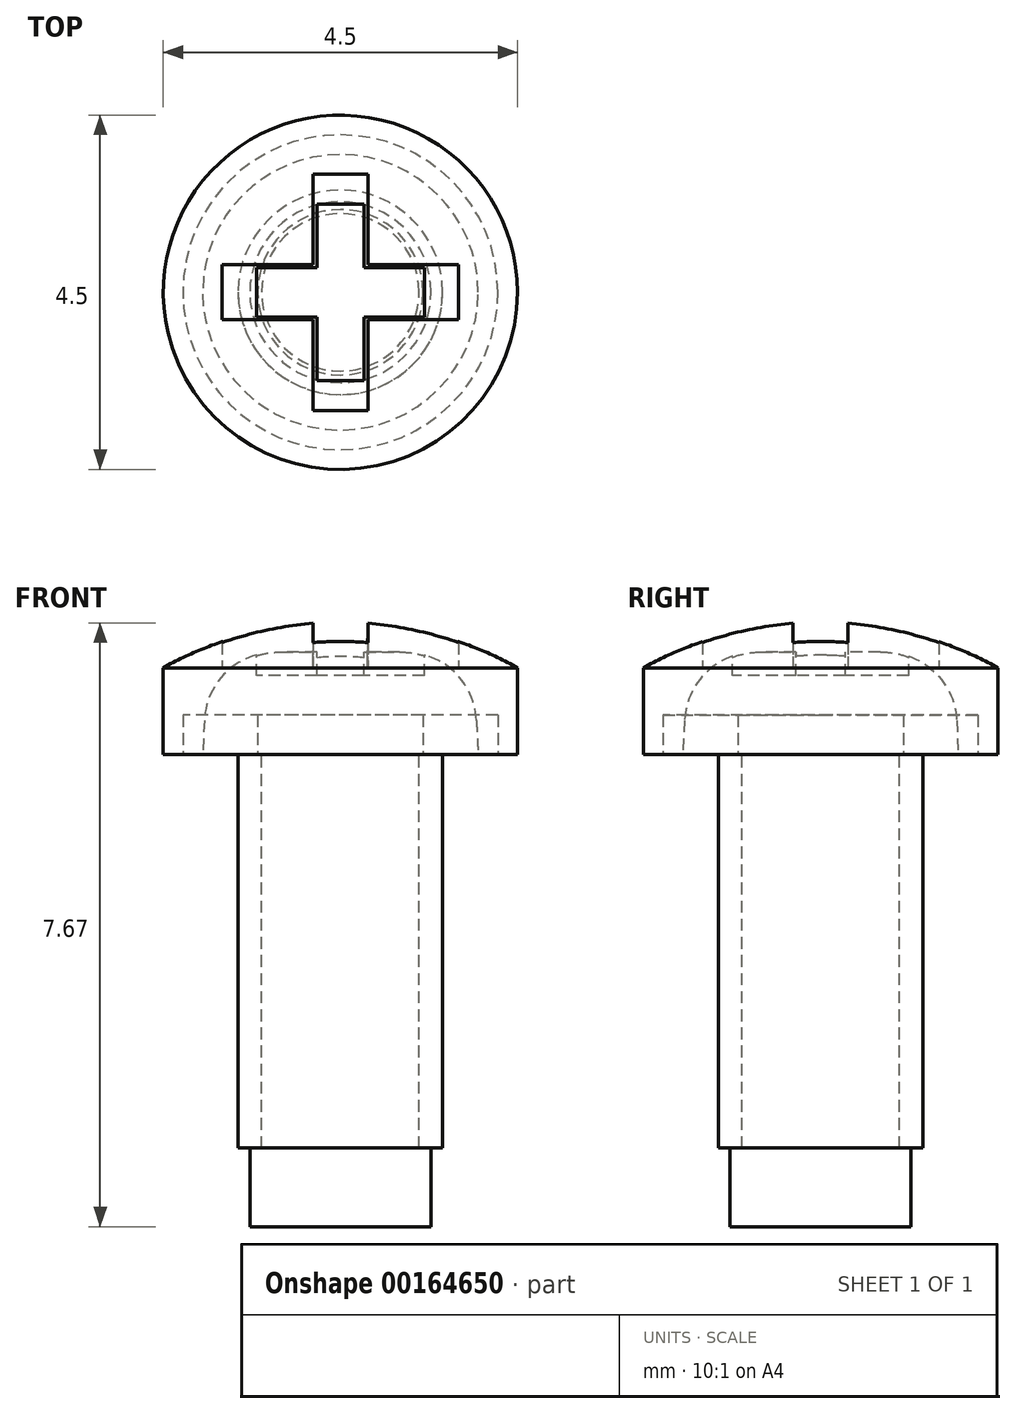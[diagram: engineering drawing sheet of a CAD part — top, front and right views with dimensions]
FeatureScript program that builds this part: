
annotation { "Feature Type Name" : "Feature", "Feature Type Description" : "" }
export const myFeature = defineFeature(function(context is Context, id is Id, definition is map)
    precondition{}
    {
        {
            var Q0;
            Q0=qCreatedBy(makeId("Front.planeOp"),FACE);
            var sketch = newSketch(context, id + "F0", { "sketchPlane" : qUnion([Q0])});
            skLineSegment(sketch, "E0", {"start": v(0, 1.5) * mm, "end": v(0, 0) * mm});
            skLineSegment(sketch, "E1", {"start": v(0, 0) * mm, "end": v(2, 0) * mm});
            skLineSegment(sketch, "E2", {"start": v(2, 0) * mm, "end": v(2, 0.7) * mm});
            skArc(sketch, "E3", {"start": v(2, 0.7) * mm, "mid": v(1.09, 1.31) * mm, "end": v(0, 1.5) * mm});
            skSolve(sketch);
        }
        {
            var Q0;
            Q0=qSketchRegion(id+"F0",true);
            var Q1;
            Q1=sQuery(id+"F0.wireOp",EDGE,"E0");
            revolve(context, id + "F1", {"entities" : qUnion([Q0]), "axis" : qUnion([Q1]), "revolveType" : RevolveType.FULL});
        }
        {
            var Q0;
            Q0=qCreatedBy(makeId("Top.planeOp"),FACE);
            cPlane(context, id + "F2", {"entities" : qUnion([Q0]), "cplaneType" : CPlaneType.OFFSET, "offset" : 1 * mm, "width" : 150 * mm, "height" : 150 * mm});
        }
        {
            var Q0;
            Q0=qCreatedBy(id+"F2.planeOp",FACE);
            var sketch = newSketch(context, id + "F3", { "sketchPlane" : qUnion([Q0])});
            skLineSegment(sketch, "E4.rect.bottom", {"start": v(0.34, 1.34) * mm, "end": v(-0.34, 1.34) * mm});
            skLineSegment(sketch, "E4.rect.top", {"start": v(0.34, -1.34) * mm, "end": v(-0.34, -1.34) * mm});
            skLineSegment(sketch, "E4.rect.left", {"start": v(0.34, 1.34) * mm, "end": v(0.34, -1.34) * mm});
            skLineSegment(sketch, "E4.rect.right", {"start": v(-0.34, 1.34) * mm, "end": v(-0.34, -1.34) * mm});
            skPoint(sketch, "E4.rect.middle", {"position": v(0, 0) * mm});
            skLineSegment(sketch, "E5.rect.bottom", {"start": v(1.32, 0.3) * mm, "end": v(-1.32, 0.3) * mm});
            skLineSegment(sketch, "E5.rect.top", {"start": v(1.32, -0.3) * mm, "end": v(-1.32, -0.3) * mm});
            skLineSegment(sketch, "E5.rect.left", {"start": v(1.32, 0.3) * mm, "end": v(1.32, -0.3) * mm});
            skLineSegment(sketch, "E5.rect.right", {"start": v(-1.32, 0.3) * mm, "end": v(-1.32, -0.3) * mm});
            skSolve(sketch);
        }
        {
            var Q0;
            Q0=qSketchRegion(id+"F3",true);
            extrude(context, id + "F4", {"entities" : qUnion([Q0]), "operationType" : NewBodyOperationType.REMOVE, "depth" : 25 * mm});
        }
        {
            var Q0;
            Q0=makeQuery(id+"F1.opRevolve","SWEPT_BODY",BODY,{"disambiguationData":[OSD([sQuery(id+"F0.wireOp",EDGE,"E0"),sQuery(id+"F0.wireOp",EDGE,"E1"),sQuery(id+"F0.wireOp",EDGE,"E2"),sQuery(id+"F0.wireOp",EDGE,"E3")])]});
            transform(context, id + "F5", {"entities" : qUnion([Q0]), "transformType" : TransformType.COPY});
        }
        {
            var Q0;
            Q0=makeQuery(id+"F1.opRevolve","SWEPT_BODY",BODY,{"disambiguationData":[OSD([sQuery(id+"F0.wireOp",EDGE,"E0"),sQuery(id+"F0.wireOp",EDGE,"E1"),sQuery(id+"F0.wireOp",EDGE,"E2"),sQuery(id+"F0.wireOp",EDGE,"E3")])]});
            transform(context, id + "F6", {"entities" : qUnion([Q0]), "transformType" : TransformType.COPY});
        }
        {
            var Q0;
            Q0=makeQuery(id+"F1.opRevolve","SWEPT_FACE",FACE,{"disambiguationData":[OSD([sQuery(id+"F0.wireOp",EDGE,"E1")])]});
            var sketch = newSketch(context, id + "F7", { "sketchPlane" : qUnion([Q0])});
            skCircle(sketch, "E6", {"center": v(0, 0) * mm, "radius": 1.15 * mm});
            skSolve(sketch);
        }
        {
            var Q0;
            Q0=qSketchRegion(id+"F7",true);
            extrude(context, id + "F8", {"entities" : qUnion([Q0]), "operationType" : NewBodyOperationType.ADD, "depth" : 5 * mm});
        }
        {
            var Q0;
            Q0=qSketchRegion(id+"F7",true);
            extrude(context, id + "F9", {"entities" : qUnion([Q0]), "operationType" : NewBodyOperationType.ADD, "depth" : 6 * mm});
        }
        {
            var Q0;
            Q0=qSketchRegion(id+"F7",true);
            extrude(context, id + "F10", {"entities" : qUnion([Q0]), "operationType" : NewBodyOperationType.ADD, "depth" : 4 * mm});
        }
        {
            var Q0;
            Q0=qCreatedBy(makeId("Front.planeOp"),FACE);
            var sketch = newSketch(context, id + "F11", { "sketchPlane" : qUnion([Q0])});
            skLineSegment(sketch, "E7", {"start": v(0, 0) * mm, "end": v(2.25, 0) * mm});
            skLineSegment(sketch, "E8", {"start": v(2.25, 0) * mm, "end": v(2.25, 1.1) * mm});
            skArc(sketch, "E9", {"start": v(2.25, 1.1) * mm, "mid": v(1.16, 1.54) * mm, "end": v(0, 1.7) * mm});
            skLineSegment(sketch, "E10", {"start": v(0, 1.7) * mm, "end": v(0, 0) * mm});
            skSolve(sketch);
        }
        {
            var Q0;
            Q0=qSketchRegion(id+"F11",true);
            var Q1;
            Q1=sQuery(id+"F11.wireOp",EDGE,"E10");
            revolve(context, id + "F12", {"entities" : qUnion([Q0]), "axis" : qUnion([Q1]), "revolveType" : RevolveType.FULL});
        }
        {
            var Q0;
            Q0=makeQuery(id+"F12.opRevolve","SWEPT_FACE",FACE,{"disambiguationData":[OSD([sQuery(id+"F11.wireOp",EDGE,"E7")])]});
            cPlane(context, id + "F13", {"entities" : qUnion([Q0]), "cplaneType" : CPlaneType.OFFSET, "offset" : 1.1 * mm, "oppositeDirection" : true, "width" : 150 * mm, "height" : 150 * mm});
        }
        {
            var Q0;
            Q0=qCreatedBy(id+"F13.planeOp",FACE);
            var sketch = newSketch(context, id + "F14", { "sketchPlane" : qUnion([Q0])});
            skLineSegment(sketch, "E11.rect.bottom", {"start": v(0.35, -1.5) * mm, "end": v(-0.35, -1.5) * mm});
            skLineSegment(sketch, "E11.rect.top", {"start": v(0.35, 1.5) * mm, "end": v(-0.35, 1.5) * mm});
            skLineSegment(sketch, "E11.rect.left", {"start": v(0.35, -1.5) * mm, "end": v(0.35, 1.5) * mm});
            skLineSegment(sketch, "E11.rect.right", {"start": v(-0.35, -1.5) * mm, "end": v(-0.35, 1.5) * mm});
            skPoint(sketch, "E11.rect.middle", {"position": v(0, 0) * mm});
            skLineSegment(sketch, "E12.rect.bottom", {"start": v(1.5, -0.35) * mm, "end": v(-1.5, -0.35) * mm});
            skLineSegment(sketch, "E12.rect.top", {"start": v(1.5, 0.35) * mm, "end": v(-1.5, 0.35) * mm});
            skLineSegment(sketch, "E12.rect.left", {"start": v(1.5, -0.35) * mm, "end": v(1.5, 0.35) * mm});
            skLineSegment(sketch, "E12.rect.right", {"start": v(-1.5, -0.35) * mm, "end": v(-1.5, 0.35) * mm});
            skSolve(sketch);
        }
        {
            var Q0;
            Q0=qSketchRegion(id+"F14",true);
            extrude(context, id + "F15", {"entities" : qUnion([Q0]), "operationType" : NewBodyOperationType.REMOVE, "oppositeDirection" : true, "depth" : 25 * mm});
        }
        {
            var Q0;
            Q0=makeQuery(id+"F12.opRevolve","SWEPT_BODY",BODY,{"disambiguationData":[OSD([sQuery(id+"F11.wireOp",EDGE,"E7"),sQuery(id+"F11.wireOp",EDGE,"E8"),sQuery(id+"F11.wireOp",EDGE,"E9"),sQuery(id+"F11.wireOp",EDGE,"E10")])]});
            transform(context, id + "F16", {"entities" : qUnion([Q0]), "transformType" : TransformType.COPY});
        }
        {
            var Q0;
            Q0=makeQuery(id+"F12.opRevolve","SWEPT_FACE",FACE,{"disambiguationData":[OSD([sQuery(id+"F11.wireOp",EDGE,"E7")])]});
            var sketch = newSketch(context, id + "F17", { "sketchPlane" : qUnion([Q0])});
            skCircle(sketch, "E13", {"center": v(0, 0) * mm, "radius": 1.3 * mm});
            skSolve(sketch);
        }
        {
            var Q0;
            Q0=qSketchRegion(id+"F17",true);
            extrude(context, id + "F18", {"entities" : qUnion([Q0]), "operationType" : NewBodyOperationType.ADD, "depth" : 4 * mm});
        }
        {
            var Q0;
            Q0=qSketchRegion(id+"F17",true);
            extrude(context, id + "F19", {"entities" : qUnion([Q0]), "operationType" : NewBodyOperationType.ADD, "depth" : 5 * mm});
        }
        {
            var Q0;
            Q0=qCreatedBy(makeId("Front.planeOp"),FACE);
            var sketch = newSketch(context, id + "F20", { "sketchPlane" : qUnion([Q0])});
            skLineSegment(sketch, "E14", {"start": v(0, 0) * mm, "end": v(1.75, 0) * mm});
            skLineSegment(sketch, "E15", {"start": v(0, 1.3) * mm, "end": v(0, 0) * mm});
            skLineSegment(sketch, "E16", {"start": v(0, 1.3) * mm, "end": v(0.82, 1.3) * mm});
            skLineSegment(sketch, "E17", {"start": v(1.75, 0) * mm, "end": v(1.73, 0.43) * mm});
            skArc(sketch, "E18", {"start": v(1.73, 0.43) * mm, "mid": v(1.45, 1.05) * mm, "end": v(0.82, 1.3) * mm});
            skLineSegment(sketch, "E19.bottom", {"start": v(0, 0) * mm, "end": v(1, 0) * mm});
            skLineSegment(sketch, "E19.top", {"start": v(0, -5) * mm, "end": v(1, -5) * mm});
            skLineSegment(sketch, "E19.left", {"start": v(0, 0) * mm, "end": v(0, -5) * mm});
            skLineSegment(sketch, "E19.right", {"start": v(1, 0) * mm, "end": v(1, -5) * mm});
            skSolve(sketch);
        }
        {
            var Q0;
            Q0=qSketchRegion(id+"F20",true);
            var Q1;
            Q1=sQuery(id+"F20.wireOp",EDGE,"E19.left");
            revolve(context, id + "F21", {"entities" : qUnion([Q0]), "axis" : qUnion([Q1]), "revolveType" : RevolveType.FULL});
        }
        {
            var Q0;
            Q0=makeQuery(id+"F21.opRevolve","SWEPT_FACE",FACE,{"disambiguationData":[OSD([sQuery(id+"F20.wireOp",EDGE,"E16")])]});
            var sketch = newSketch(context, id + "F22", { "sketchPlane" : qUnion([Q0])});
            skLineSegment(sketch, "E20.bottom", {"start": v(0.3, 1.12) * mm, "end": v(-0.3, 1.12) * mm});
            skLineSegment(sketch, "E20.top", {"start": v(0.3, -1.12) * mm, "end": v(-0.3, -1.12) * mm});
            skLineSegment(sketch, "E20.left", {"start": v(0.3, 1.12) * mm, "end": v(0.3, -1.12) * mm});
            skLineSegment(sketch, "E20.right", {"start": v(-0.3, 1.12) * mm, "end": v(-0.3, -1.12) * mm});
            skPoint(sketch, "E20.middle", {"position": v(0, 0) * mm});
            skLineSegment(sketch, "E21.bottom", {"start": v(1.07, 0.31) * mm, "end": v(-1.07, 0.31) * mm});
            skLineSegment(sketch, "E21.top", {"start": v(1.07, -0.31) * mm, "end": v(-1.07, -0.31) * mm});
            skLineSegment(sketch, "E21.left", {"start": v(1.07, 0.31) * mm, "end": v(1.07, -0.31) * mm});
            skLineSegment(sketch, "E21.right", {"start": v(-1.07, 0.31) * mm, "end": v(-1.07, -0.31) * mm});
            skSolve(sketch);
        }
        {
            var Q0;
            Q0=qSketchRegion(id+"F22",true);
            extrude(context, id + "F23", {"entities" : qUnion([Q0]), "operationType" : NewBodyOperationType.REMOVE, "oppositeDirection" : true, "depth" : 0.3 * mm});
        }
        {
            var Q0;
            Q0=qCreatedBy(makeId("Top.planeOp"),FACE);
            var sketch = newSketch(context, id + "F24", { "sketchPlane" : qUnion([Q0])});
            skCircle(sketch, "E22", {"center": v(0, 0) * mm, "radius": 2 * mm});
            skCircle(sketch, "E23", {"center": v(0, 0) * mm, "radius": 1.05 * mm});
            skSolve(sketch);
        }
        {
            var Q0;
            Q0=qSketchRegion(id+"F24",true);
            extrude(context, id + "F25", {"entities" : qUnion([Q0]), "depth" : 0.5 * mm});
        }
    });
